# Revit family: CITY ALPHABET litera „S”
name_source: partatom
category: Meble
revit_build: Autodesk Revit 2018 (Build: 20190510_1515(x64)
units: mm (PartAtom-declared; Revit-internal decimal feet)

## family parameters
Numer OmniClass = 23.40.10.11.14
Obiekt nadrzędny = Powierzchnia
Punkt obliczania pomieszczeń = Nie
Tnij formami wycięć po wczytaniu = Nie
Tytuł OmniClass = Exterior Seating
Współdzielony = Nie

## types (1)
- CITY ALPHABET litera „S”
    Domyślna rzędna = 1219 mm
    Długość = 3900 mm  [stored 12.7953 ft]
    IfcExportAs = IfcFurnishingElement
    Komentarze do typu = Ławka
    Materiał - informacja = Szeroki wybór kolorów wg palety RAL. Istnieje również możliwość specjalnego wykonania
kolorystycznego na indywidualne zapytanie klienta.
    Model = CITY ALPHABET litera „S”
    Obraz typu = S.jpg
    Producent = Astrini Design
    Szerokość = 2350 mm
    Temepratura użytkowania = -40°C do 80°C, ( -40°F do 176°F )
    URL = http://astrini-design.pl
    Waga (szacunkowo) = 112.00 kg
    Waga po wypełnieniu (szacunkowo) = 252.00 kg
    Wysokość = 420 mm  [stored 1.37795 ft]

note: [stored X ft] marks values corroborated as IEEE doubles in the binary element streams (Revit-internal decimal feet)
